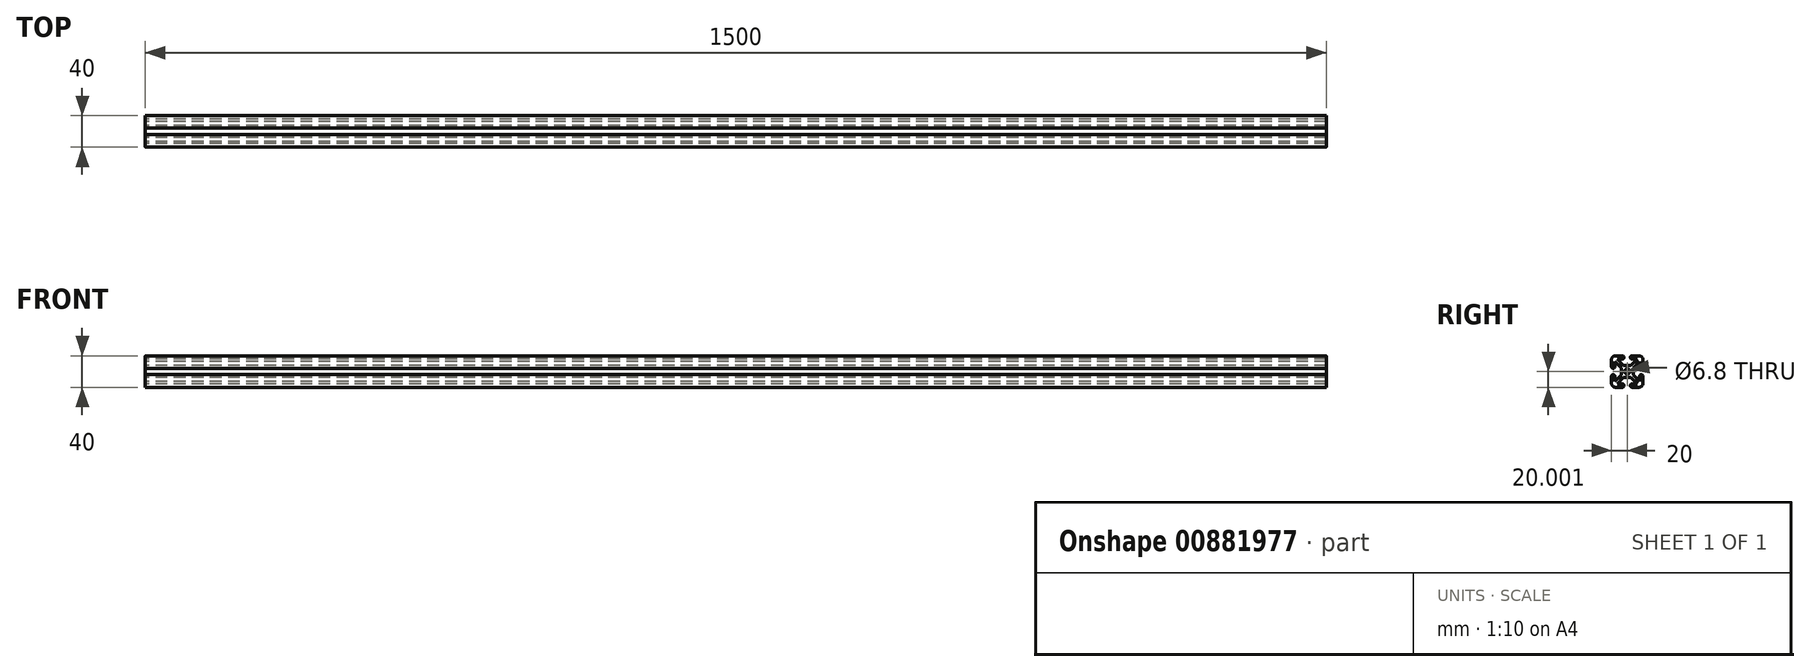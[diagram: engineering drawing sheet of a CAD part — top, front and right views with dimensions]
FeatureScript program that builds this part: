
annotation { "Feature Type Name" : "Feature", "Feature Type Description" : "" }
export const myFeature = defineFeature(function(context is Context, id is Id, definition is map)
    precondition{}
    {
        {
            var Q0;
            Q0=qCreatedBy(makeId("Right.planeOp"),FACE);
            var sketch = newSketch(context, id + "F0", { "sketchPlane" : qUnion([Q0])});
            skLineSegment(sketch, "E0", {"start": v(-15.94, 15.35) * mm, "end": v(0, 15.35) * mm});
            skLineSegment(sketch, "E1", {"start": v(0, 15.35) * mm, "end": v(8.12, 15.35) * mm, "construction": true});
            skLineSegment(sketch, "E2", {"start": v(8.12, 15.35) * mm, "end": v(24.06, 15.35) * mm});
            skLineSegment(sketch, "E3.bottom", {"start": v(-3.62, 3.04) * mm, "end": v(11.75, 3.04) * mm});
            skLineSegment(sketch, "E3.top", {"start": v(-3.62, -12.33) * mm, "end": v(11.75, -12.33) * mm});
            skLineSegment(sketch, "E3.left", {"start": v(-3.62, 3.04) * mm, "end": v(-3.62, -12.33) * mm});
            skLineSegment(sketch, "E3.right", {"start": v(11.75, 3.04) * mm, "end": v(11.75, -12.33) * mm});
            skLineSegment(sketch, "E4", {"start": v(11.74, 3.04) * mm, "end": v(24.06, 15.35) * mm, "construction": true});
            skLineSegment(sketch, "E5", {"start": v(-3.62, 3.04) * mm, "end": v(-15.94, 15.35) * mm});
            skLineSegment(sketch, "E6", {"start": v(-3.62, -12.33) * mm, "end": v(-15.94, -24.65) * mm, "construction": true});
            skLineSegment(sketch, "E7", {"start": v(11.74, -12.33) * mm, "end": v(24.06, -24.65) * mm});
            skLineSegment(sketch, "E8", {"start": v(16.5, 7.78) * mm, "end": v(14.97, 9.31) * mm, "construction": true});
            skLineSegment(sketch, "E9", {"start": v(16.5, 7.78) * mm, "end": v(18.02, 6.26) * mm, "construction": true});
            skLineSegment(sketch, "E10", {"start": v(14.97, 9.31) * mm, "end": v(21, 15.35) * mm});
            skLineSegment(sketch, "E11", {"start": v(18.02, 6.26) * mm, "end": v(24.06, 12.3) * mm});
            skLineSegment(sketch, "E12", {"start": v(14.97, 9.31) * mm, "end": v(-15.94, -21.6) * mm});
            skLineSegment(sketch, "E13", {"start": v(18.02, 6.26) * mm, "end": v(-12.89, -24.65) * mm});
            skLineSegment(sketch, "E14", {"start": v(0, 15.35) * mm, "end": v(0, 11.03) * mm});
            skLineSegment(sketch, "E15", {"start": v(8.12, 15.35) * mm, "end": v(8.12, 11.03) * mm});
            skLineSegment(sketch, "E16", {"start": v(8.12, 11.03) * mm, "end": v(16.69, 11.03) * mm});
            skLineSegment(sketch, "E17", {"start": v(0, 11.03) * mm, "end": v(-11.62, 11.03) * mm});
            skLineSegment(sketch, "E18", {"start": v(-3.62, 3.04) * mm, "end": v(11.75, -12.33) * mm});
            skLineSegment(sketch, "E19", {"start": v(11.74, 3.04) * mm, "end": v(-3.62, -12.33) * mm, "construction": true});
            skCircle(sketch, "E20", {"center": v(4.06, -4.65) * mm, "radius": 3.4 * mm});
            skLineSegment(sketch, "E21", {"start": v(24.06, -0.59) * mm, "end": v(24.06, -8.7) * mm, "construction": true});
            skLineSegment(sketch, "E22", {"start": v(24.06, -0.59) * mm, "end": v(24.06, 15.35) * mm});
            skLineSegment(sketch, "E23", {"start": v(24.06, -24.65) * mm, "end": v(24.06, -8.7) * mm});
            skLineSegment(sketch, "E24", {"start": v(24.06, -0.59) * mm, "end": v(19.74, -0.59) * mm});
            skLineSegment(sketch, "E25", {"start": v(24.06, -8.7) * mm, "end": v(19.74, -8.7) * mm});
            skLineSegment(sketch, "E26", {"start": v(19.74, -0.59) * mm, "end": v(19.74, 7.98) * mm});
            skLineSegment(sketch, "E27", {"start": v(19.74, 7.98) * mm, "end": v(16.69, 11.03) * mm});
            skLineSegment(sketch, "E28", {"start": v(-7.27, 6.68) * mm, "end": v(-8.8, 5.15) * mm});
            skLineSegment(sketch, "E29", {"start": v(-7.27, 6.68) * mm, "end": v(-5.74, 8.2) * mm});
            skLineSegment(sketch, "E30", {"start": v(-5.74, 8.2) * mm, "end": v(-12.89, 15.35) * mm});
            skLineSegment(sketch, "E31", {"start": v(-5.74, 8.2) * mm, "end": v(24.06, -21.6) * mm});
            skLineSegment(sketch, "E32", {"start": v(19.74, -8.7) * mm, "end": v(19.74, -17.27) * mm});
            skLineSegment(sketch, "E33", {"start": v(-15.94, 15.35) * mm, "end": v(-15.94, -0.59) * mm});
            skLineSegment(sketch, "E34", {"start": v(-15.94, -0.59) * mm, "end": v(-15.94, -8.7) * mm, "construction": true});
            skLineSegment(sketch, "E35", {"start": v(-15.94, -24.65) * mm, "end": v(0, -24.65) * mm});
            skLineSegment(sketch, "E36", {"start": v(0, -24.65) * mm, "end": v(8.12, -24.65) * mm, "construction": true});
            skLineSegment(sketch, "E37", {"start": v(-15.94, -8.7) * mm, "end": v(-15.94, -24.65) * mm});
            skLineSegment(sketch, "E38", {"start": v(8.12, -24.65) * mm, "end": v(24.06, -24.65) * mm});
            skLineSegment(sketch, "E39", {"start": v(-8.8, 5.15) * mm, "end": v(-15.94, 12.3) * mm});
            skLineSegment(sketch, "E40", {"start": v(-8.8, 5.15) * mm, "end": v(21, -24.65) * mm});
            skLineSegment(sketch, "E41", {"start": v(-15.94, -0.59) * mm, "end": v(-11.62, -0.59) * mm});
            skLineSegment(sketch, "E42", {"start": v(-15.94, -8.7) * mm, "end": v(-11.62, -8.7) * mm});
            skLineSegment(sketch, "E43", {"start": v(0, -24.65) * mm, "end": v(0, -20.33) * mm});
            skLineSegment(sketch, "E44", {"start": v(8.12, -24.65) * mm, "end": v(8.12, -20.33) * mm});
            skLineSegment(sketch, "E45", {"start": v(-11.62, -0.59) * mm, "end": v(-11.62, 7.98) * mm});
            skLineSegment(sketch, "E46", {"start": v(-11.62, -8.7) * mm, "end": v(-11.62, -17.27) * mm});
            skLineSegment(sketch, "E47", {"start": v(0, -20.33) * mm, "end": v(-8.57, -20.33) * mm});
            skLineSegment(sketch, "E48", {"start": v(8.12, -20.33) * mm, "end": v(16.69, -20.33) * mm});
            skSolve(sketch);
        }
        {
            var Q0;
            {var subQ0=sQuery(id+"F0.wireOp",EDGE,"E41");Q0=makeQuery(id+"F0.imprint","IMPRINT",FACE,{"disambiguationData":[TD([[makeQuery(id+"F0.imprint","IMPRINT",EDGE,{"derivedFrom":subQ0}),1.0]])]});}
            var Q1;
            {var subQ0=sQuery(id+"F0.wireOp",EDGE,"E28");Q1=makeQuery(id+"F0.imprint","IMPRINT",FACE,{"disambiguationData":[TD([[makeQuery(id+"F0.imprint","IMPRINT",EDGE,{"derivedFrom":subQ0}),-1.0]])]});}
            var Q2;
            {var subQ3=sQuery(id+"F0.wireOp",EDGE,"E29");Q2=makeQuery(id+"F0.imprint","IMPRINT",FACE,{"disambiguationData":[TD([[makeQuery(id+"F0.imprint","IMPRINT",EDGE,{"derivedFrom":subQ3}),1.0]])]});}
            var Q3;
            {var subQ0=sQuery(id+"F0.wireOp",EDGE,"E14");Q3=makeQuery(id+"F0.imprint","IMPRINT",FACE,{"disambiguationData":[TD([[makeQuery(id+"F0.imprint","IMPRINT",EDGE,{"derivedFrom":subQ0}),-1.0]])]});}
            var Q4;
            {var subQ0=sQuery(id+"F0.wireOp",EDGE,"E5");var subQ5=sQuery(id+"F0.wireOp",EDGE,"E17");var subQ6=makeQuery(id+"F0.imprint","INTERSECT",VERTEX,{"derivedFrom":[subQ0,subQ5]});Q4=makeQuery(id+"F0.imprint","IMPRINT",FACE,{"disambiguationData":[TD([[makeQuery(id+"F0.imprint","IMPRINT",EDGE,{"disambiguationData":[TD([[subQ6,1.0]])],"derivedFrom":subQ5}),-1.0]])]});}
            var Q5;
            {var subQ4=sQuery(id+"F0.wireOp",EDGE,"E42");Q5=makeQuery(id+"F0.imprint","IMPRINT",FACE,{"disambiguationData":[TD([[makeQuery(id+"F0.imprint","IMPRINT",EDGE,{"derivedFrom":subQ4}),-1.0]])]});}
            var Q6;
            {var subQ2=sQuery(id+"F0.wireOp",EDGE,"E3.left");var subQ6=sQuery(id+"F0.wireOp",EDGE,"E3.top");var subQ7=makeQuery(id+"F0.imprint","INTERSECT",VERTEX,{"derivedFrom":[subQ6,subQ2]});Q6=makeQuery(id+"F0.imprint","IMPRINT",FACE,{"disambiguationData":[TD([[makeQuery(id+"F0.imprint","IMPRINT",EDGE,{"disambiguationData":[TD([[subQ7,-1.0]])],"derivedFrom":subQ6}),-1.0]])]});}
            var Q7;
            {var subQ4=sQuery(id+"F0.wireOp",EDGE,"E43");Q7=makeQuery(id+"F0.imprint","IMPRINT",FACE,{"disambiguationData":[TD([[makeQuery(id+"F0.imprint","IMPRINT",EDGE,{"derivedFrom":subQ4}),1.0]])]});}
            var Q8;
            {var subQ3=sQuery(id+"F0.wireOp",EDGE,"E27");Q8=makeQuery(id+"F0.imprint","IMPRINT",FACE,{"disambiguationData":[TD([[makeQuery(id+"F0.imprint","IMPRINT",EDGE,{"derivedFrom":subQ3}),1.0]])]});}
            var Q9;
            {var subQ3=sQuery(id+"F0.wireOp",EDGE,"E27");Q9=makeQuery(id+"F0.imprint","IMPRINT",FACE,{"disambiguationData":[TD([[makeQuery(id+"F0.imprint","IMPRINT",EDGE,{"derivedFrom":subQ3}),-1.0]])]});}
            var Q10;
            {var subQ4=sQuery(id+"F0.wireOp",EDGE,"E24");Q10=makeQuery(id+"F0.imprint","IMPRINT",FACE,{"disambiguationData":[TD([[makeQuery(id+"F0.imprint","IMPRINT",EDGE,{"derivedFrom":subQ4}),-1.0]])]});}
            var Q11;
            {var subQ0=sQuery(id+"F0.wireOp",EDGE,"E15");Q11=makeQuery(id+"F0.imprint","IMPRINT",FACE,{"disambiguationData":[TD([[makeQuery(id+"F0.imprint","IMPRINT",EDGE,{"derivedFrom":subQ0}),1.0]])]});}
            var Q12;
            {var subQ0=sQuery(id+"F0.wireOp",EDGE,"E13");var subQ1=sQuery(id+"F0.wireOp",EDGE,"E3.right");var subQ2=makeQuery(id+"F0.imprint","INTERSECT",VERTEX,{"derivedFrom":[subQ1,subQ0]});Q12=makeQuery(id+"F0.imprint","IMPRINT",FACE,{"disambiguationData":[TD([[makeQuery(id+"F0.imprint","IMPRINT",EDGE,{"disambiguationData":[TD([[subQ2,-1.0]])],"derivedFrom":subQ1}),-1.0]])]});}
            var Q13;
            {var subQ0=sQuery(id+"F0.wireOp",EDGE,"E13");var subQ1=sQuery(id+"F0.wireOp",EDGE,"E3.top");var subQ2=makeQuery(id+"F0.imprint","INTERSECT",VERTEX,{"derivedFrom":[subQ1,subQ0]});Q13=makeQuery(id+"F0.imprint","IMPRINT",FACE,{"disambiguationData":[TD([[makeQuery(id+"F0.imprint","IMPRINT",EDGE,{"disambiguationData":[TD([[subQ2,-1.0]])],"derivedFrom":subQ1}),1.0]])]});}
            var Q14;
            {var subQ0=sQuery(id+"F0.wireOp",EDGE,"E40");var subQ1=sQuery(id+"F0.wireOp",EDGE,"E3.left");var subQ2=makeQuery(id+"F0.imprint","INTERSECT",VERTEX,{"derivedFrom":[subQ1,subQ0]});Q14=makeQuery(id+"F0.imprint","IMPRINT",FACE,{"disambiguationData":[TD([[makeQuery(id+"F0.imprint","IMPRINT",EDGE,{"disambiguationData":[TD([[subQ2,-1.0]])],"derivedFrom":subQ1}),1.0]])]});}
            var Q15;
            {var subQ0=sQuery(id+"F0.wireOp",EDGE,"E31");var subQ1=sQuery(id+"F0.wireOp",EDGE,"E3.bottom");var subQ2=makeQuery(id+"F0.imprint","INTERSECT",VERTEX,{"derivedFrom":[subQ1,subQ0]});Q15=makeQuery(id+"F0.imprint","IMPRINT",FACE,{"disambiguationData":[TD([[makeQuery(id+"F0.imprint","IMPRINT",EDGE,{"disambiguationData":[TD([[subQ2,-1.0]])],"derivedFrom":subQ1}),-1.0]])]});}
            var Q16;
            {var subQ5=sQuery(id+"F0.wireOp",EDGE,"E29");Q16=makeQuery(id+"F0.imprint","IMPRINT",FACE,{"disambiguationData":[TD([[makeQuery(id+"F0.imprint","IMPRINT",EDGE,{"derivedFrom":subQ5}),-1.0]])]});}
            var Q17;
            {var subQ5=sQuery(id+"F0.wireOp",EDGE,"E28");Q17=makeQuery(id+"F0.imprint","IMPRINT",FACE,{"disambiguationData":[TD([[makeQuery(id+"F0.imprint","IMPRINT",EDGE,{"derivedFrom":subQ5}),1.0]])]});}
            var Q18;
            {var subQ1=sQuery(id+"F0.wireOp",EDGE,"E7");Q18=makeQuery(id+"F0.imprint","IMPRINT",FACE,{"disambiguationData":[TD([[makeQuery(id+"F0.imprint","IMPRINT",EDGE,{"derivedFrom":subQ1}),-1.0]])]});}
            var Q19;
            {var subQ1=sQuery(id+"F0.wireOp",EDGE,"E7");Q19=makeQuery(id+"F0.imprint","IMPRINT",FACE,{"disambiguationData":[TD([[makeQuery(id+"F0.imprint","IMPRINT",EDGE,{"derivedFrom":subQ1}),1.0]])]});}
            var Q20;
            {var subQ0=sQuery(id+"F0.wireOp",EDGE,"E25");Q20=makeQuery(id+"F0.imprint","IMPRINT",FACE,{"disambiguationData":[TD([[makeQuery(id+"F0.imprint","IMPRINT",EDGE,{"derivedFrom":subQ0}),1.0]])]});}
            var Q21;
            {var subQ0=sQuery(id+"F0.wireOp",EDGE,"E44");Q21=makeQuery(id+"F0.imprint","IMPRINT",FACE,{"disambiguationData":[TD([[makeQuery(id+"F0.imprint","IMPRINT",EDGE,{"derivedFrom":subQ0}),-1.0]])]});}
            var Q22;
            {var subQ1=sQuery(id+"F0.wireOp",EDGE,"E3.right");var subQ6=sQuery(id+"F0.wireOp",EDGE,"E3.bottom");var subQ9=makeQuery(id+"F0.imprint","INTERSECT",VERTEX,{"derivedFrom":[subQ6,subQ1]});Q22=makeQuery(id+"F0.imprint","IMPRINT",FACE,{"disambiguationData":[TD([[makeQuery(id+"F0.imprint","IMPRINT",EDGE,{"disambiguationData":[TD([[subQ9,1.0]])],"derivedFrom":subQ6}),-1.0]])]});}
            var Q23;
            {var subQ0=sQuery(id+"F0.wireOp",EDGE,"E18");var subQ5=sQuery(id+"F0.wireOp",EDGE,"E20");var subQ6=makeQuery(id+"F0.imprint","INTERSECT",VERTEX,{"disambiguationData":[OD(0.0)],"derivedFrom":[subQ0,subQ5]});Q23=makeQuery(id+"F0.imprint","IMPRINT",FACE,{"disambiguationData":[TD([[makeQuery(id+"F0.imprint","IMPRINT",EDGE,{"disambiguationData":[TD([[subQ6,-1.0]])],"derivedFrom":subQ5}),-1.0]])]});}
            var Q24;
            {var subQ1=sQuery(id+"F0.wireOp",EDGE,"E3.top");var subQ6=sQuery(id+"F0.wireOp",EDGE,"E3.left");var subQ9=makeQuery(id+"F0.imprint","INTERSECT",VERTEX,{"derivedFrom":[subQ1,subQ6]});Q24=makeQuery(id+"F0.imprint","IMPRINT",FACE,{"disambiguationData":[TD([[makeQuery(id+"F0.imprint","IMPRINT",EDGE,{"disambiguationData":[TD([[subQ9,-1.0]])],"derivedFrom":subQ1}),1.0]])]});}
            var Q25;
            {var subQ0=sQuery(id+"F0.wireOp",EDGE,"E18");var subQ5=sQuery(id+"F0.wireOp",EDGE,"E20");var subQ6=makeQuery(id+"F0.imprint","INTERSECT",VERTEX,{"disambiguationData":[OD(1.0)],"derivedFrom":[subQ0,subQ5]});Q25=makeQuery(id+"F0.imprint","IMPRINT",FACE,{"disambiguationData":[TD([[makeQuery(id+"F0.imprint","IMPRINT",EDGE,{"disambiguationData":[TD([[subQ6,1.0]])],"derivedFrom":subQ5}),-1.0]])]});}
            var Q26;
            {var subQ0=sQuery(id+"F0.wireOp",EDGE,"E18");var subQ5=sQuery(id+"F0.wireOp",EDGE,"E20");var subQ6=makeQuery(id+"F0.imprint","INTERSECT",VERTEX,{"disambiguationData":[OD(1.0)],"derivedFrom":[subQ0,subQ5]});Q26=makeQuery(id+"F0.imprint","IMPRINT",FACE,{"disambiguationData":[TD([[makeQuery(id+"F0.imprint","IMPRINT",EDGE,{"disambiguationData":[TD([[subQ6,-1.0]])],"derivedFrom":subQ5}),-1.0]])]});}
            var Q27;
            {var subQ0=sQuery(id+"F0.wireOp",EDGE,"E18");var subQ5=sQuery(id+"F0.wireOp",EDGE,"E20");var subQ6=makeQuery(id+"F0.imprint","INTERSECT",VERTEX,{"disambiguationData":[OD(0.0)],"derivedFrom":[subQ0,subQ5]});Q27=makeQuery(id+"F0.imprint","IMPRINT",FACE,{"disambiguationData":[TD([[makeQuery(id+"F0.imprint","IMPRINT",EDGE,{"disambiguationData":[TD([[subQ6,1.0]])],"derivedFrom":subQ5}),-1.0]])]});}
            extrude(context, id + "F1", {"entities" : qUnion([Q0, Q1, Q2, Q3, Q4, Q5, Q6, Q7, Q8, Q9, Q10, Q11, Q12, Q13, Q14, Q15, Q16, Q17, Q18, Q19, Q20, Q21, Q22, Q23, Q24, Q25, Q26, Q27]), "offsetDistance" : 25 * mm, "depth" : 1500 * mm});
        }
        {
            var Q0;
            Q0=makeQuery(id+"F1.opExtrude","SWEPT_EDGE",EDGE,{"disambiguationData":[OSD([sQuery(id+"F0.wireOp",EDGE,"E14"),sQuery(id+"F0.wireOp",EDGE,"E17")])]});
            var Q1;
            Q1=makeQuery(id+"F1.opExtrude","SWEPT_EDGE",EDGE,{"disambiguationData":[OSD([sQuery(id+"F0.wireOp",EDGE,"E41"),sQuery(id+"F0.wireOp",EDGE,"E45")])]});
            var Q2;
            Q2=makeQuery(id+"F1.opExtrude","SWEPT_EDGE",EDGE,{"disambiguationData":[OSD([sQuery(id+"F0.wireOp",EDGE,"E33"),sQuery(id+"F0.wireOp",EDGE,"E41")])]});
            var Q3;
            Q3=makeQuery(id+"F1.opExtrude","SWEPT_EDGE",EDGE,{"disambiguationData":[OSD([sQuery(id+"F0.wireOp",EDGE,"E0"),sQuery(id+"F0.wireOp",EDGE,"E14")])]});
            var Q4;
            Q4=makeQuery(id+"F1.opExtrude","SWEPT_EDGE",EDGE,{"disambiguationData":[OSD([sQuery(id+"F0.wireOp",EDGE,"E15"),sQuery(id+"F0.wireOp",EDGE,"E16")])]});
            var Q5;
            Q5=makeQuery(id+"F1.opExtrude","SWEPT_EDGE",EDGE,{"disambiguationData":[OSD([sQuery(id+"F0.wireOp",EDGE,"E24"),sQuery(id+"F0.wireOp",EDGE,"E26")])]});
            var Q6;
            Q6=makeQuery(id+"F1.opExtrude","SWEPT_EDGE",EDGE,{"disambiguationData":[OSD([sQuery(id+"F0.wireOp",EDGE,"E22"),sQuery(id+"F0.wireOp",EDGE,"E24")])]});
            var Q7;
            Q7=makeQuery(id+"F1.opExtrude","SWEPT_EDGE",EDGE,{"disambiguationData":[OSD([sQuery(id+"F0.wireOp",EDGE,"E38"),sQuery(id+"F0.wireOp",EDGE,"E44")])]});
            var Q8;
            Q8=makeQuery(id+"F1.opExtrude","SWEPT_EDGE",EDGE,{"disambiguationData":[OSD([sQuery(id+"F0.wireOp",EDGE,"E2"),sQuery(id+"F0.wireOp",EDGE,"E15")])]});
            var Q9;
            Q9=makeQuery(id+"F1.opExtrude","SWEPT_EDGE",EDGE,{"disambiguationData":[OSD([sQuery(id+"F0.wireOp",EDGE,"E37"),sQuery(id+"F0.wireOp",EDGE,"E42")])]});
            var Q10;
            Q10=makeQuery(id+"F1.opExtrude","SWEPT_EDGE",EDGE,{"disambiguationData":[OSD([sQuery(id+"F0.wireOp",EDGE,"E42"),sQuery(id+"F0.wireOp",EDGE,"E46")])]});
            var Q11;
            Q11=makeQuery(id+"F1.opExtrude","SWEPT_EDGE",EDGE,{"disambiguationData":[OSD([sQuery(id+"F0.wireOp",EDGE,"E35"),sQuery(id+"F0.wireOp",EDGE,"E43")])]});
            var Q12;
            Q12=makeQuery(id+"F1.opExtrude","SWEPT_EDGE",EDGE,{"disambiguationData":[OSD([sQuery(id+"F0.wireOp",EDGE,"E43"),sQuery(id+"F0.wireOp",EDGE,"E47")])]});
            var Q13;
            Q13=makeQuery(id+"F1.opExtrude","SWEPT_EDGE",EDGE,{"disambiguationData":[OSD([sQuery(id+"F0.wireOp",EDGE,"E44"),sQuery(id+"F0.wireOp",EDGE,"E48")])]});
            var Q14;
            Q14=makeQuery(id+"F1.opExtrude","SWEPT_EDGE",EDGE,{"disambiguationData":[OSD([sQuery(id+"F0.wireOp",EDGE,"E25"),sQuery(id+"F0.wireOp",EDGE,"E32")])]});
            var Q15;
            Q15=makeQuery(id+"F1.opExtrude","SWEPT_EDGE",EDGE,{"disambiguationData":[OSD([sQuery(id+"F0.wireOp",EDGE,"E23"),sQuery(id+"F0.wireOp",EDGE,"E25")])]});
            fillet(context, id + "F2", {"entities" : qUnion([Q0, Q1, Q2, Q3, Q4, Q5, Q6, Q7, Q8, Q9, Q10, Q11, Q12, Q13, Q14, Q15]), "radius" : 2 * mm, "tangentPropagation" : true, "allowEdgeOverflow" : false});
        }
        {
            var Q0;
            Q0=makeQuery(id+"F1.opExtrude","SWEPT_EDGE",EDGE,{"disambiguationData":[OSD([sQuery(id+"F0.wireOp",EDGE,"E0"),sQuery(id+"F0.wireOp",EDGE,"E5"),sQuery(id+"F0.wireOp",EDGE,"E33")])]});
            var Q1;
            Q1=makeQuery(id+"F1.opExtrude","SWEPT_EDGE",EDGE,{"disambiguationData":[OSD([sQuery(id+"F0.wireOp",EDGE,"E2"),sQuery(id+"F0.wireOp",EDGE,"E22")])]});
            var Q2;
            Q2=makeQuery(id+"F1.opExtrude","SWEPT_EDGE",EDGE,{"disambiguationData":[OSD([sQuery(id+"F0.wireOp",EDGE,"E7"),sQuery(id+"F0.wireOp",EDGE,"E23"),sQuery(id+"F0.wireOp",EDGE,"E38")])]});
            var Q3;
            Q3=makeQuery(id+"F1.opExtrude","SWEPT_EDGE",EDGE,{"disambiguationData":[OSD([sQuery(id+"F0.wireOp",EDGE,"E35"),sQuery(id+"F0.wireOp",EDGE,"E37")])]});
            fillet(context, id + "F3", {"entities" : qUnion([Q0, Q1, Q2, Q3]), "radius" : 5 * mm, "tangentPropagation" : true, "allowEdgeOverflow" : false});
        }
    });
